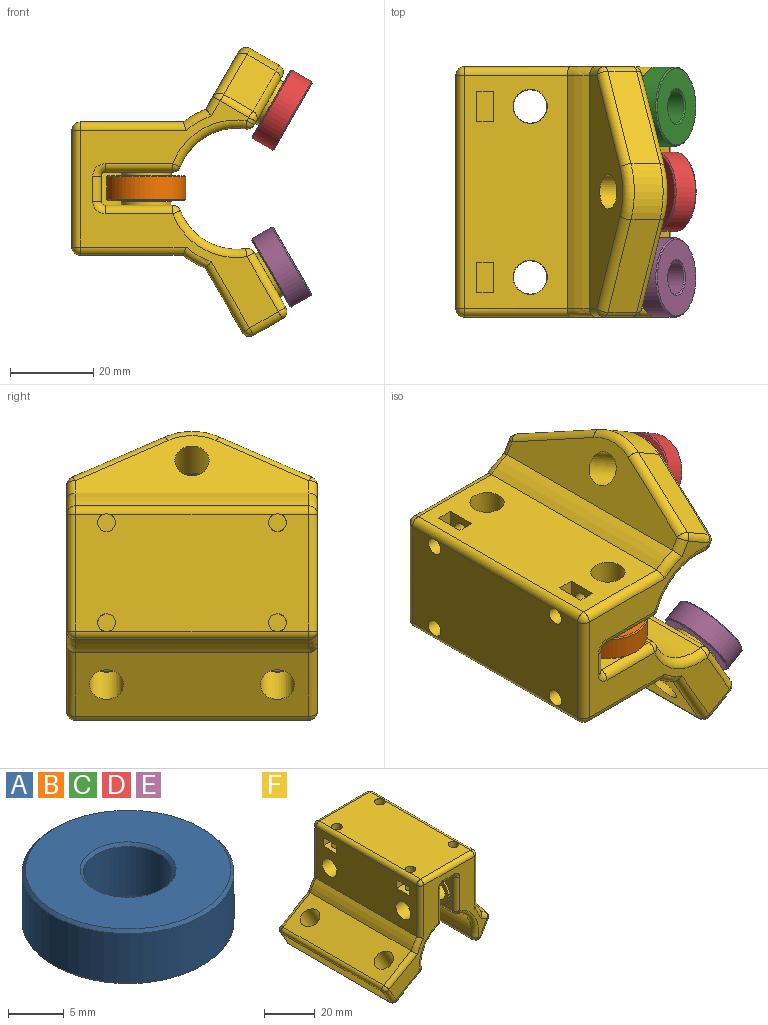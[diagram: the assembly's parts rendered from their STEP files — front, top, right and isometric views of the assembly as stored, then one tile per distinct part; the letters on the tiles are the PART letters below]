
ASSEMBLY  parts=6 mates=5
PART A: 8 faces, bbox 19x19x6 mm
  f0: cylinder r=4mm len=8mm, axis (0,0,-1), area 135.7mm2, adj f4,f6
  f1: cylinder r=9.5mm len=19mm, axis (0,0,-1), area 322.3mm2, adj f5,f7
  f2: plane 18.4x18.4mm, normal (0,0,1), area 207.8mm2, adj f6,f7
  f3: plane 18.4x18.4mm, normal (0,0,-1), area 207.8mm2, adj f4,f5
  f4: cone r=4.3mm half-angle=45deg, axis (0,0,-1), area 11.1mm2, adj f0,f3
  f5: cone r=9.5mm half-angle=45deg, axis (0,0,1), area 24.9mm2, adj f1,f3
  f6: cone r=4mm half-angle=45deg, axis (0,0,1), area 11.1mm2, adj f0,f2
  f7: cone r=9.2mm half-angle=45deg, axis (0,0,-1), area 24.9mm2, adj f1,f2
PART B: same geometry as A
PART C: same geometry as A
PART D: same geometry as A
PART E: same geometry as A
PART F: 155 faces, bbox 70.3x60x51.5 mm
  f0: plane 54.5x47.54mm, normal (0,1,0), area 621.5mm2, adj f104,f108,f112,f114,f115,f117,f118,f119
  f1: plane 54.5x47.54mm, normal (0,-1,0), area 621.5mm2, adj f83,f84,f86,f87,f88,f89,f90,f91
  f2: plane 56x28mm, normal (0,0,1), area 1511.7mm2, adj f67,f68,f73,f74,f97,f124,f144,f147
  f3: plane 56x24.66mm, normal (-1,0,0), area 1217.6mm2, adj f14,f24,f25,f55,f56,f57,f58,f60
  f4: plane 56x24.71mm, normal (1,0,0), area 1220.6mm2, adj f13,f22,f23,f45,f46,f47,f48,f50
  f5: plane 14.58x6mm, normal (0,0,-1), area 87.5mm2, adj f6,f31,f32,f88
  f6: cylinder r=1mm len=15.13mm, axis (0,-1,0), area 23.2mm2, adj f5,f8,f32,f90
  f7: cylinder r=1mm len=15.13mm, axis (0,1,0), area 23.2mm2, adj f9,f17,f32,f119
  f8: plane 56x16.13mm, normal (1,0,0), area 544mm2, adj f6,f27,f30,f32,f41,f43,f92,f112
  f9: plane 56x16.13mm, normal (-1,0,0), area 544mm2, adj f7,f28,f31,f32,f37,f39,f84,f121
  f10: plane 56x15.34mm, normal (-0.5,0,0.87), area 886.2mm2, adj f14,f20,f21,f105,f113,f118
  f11: plane 56x13.11mm, normal (0.5,0,-0.87), area 621.5mm2, adj f26,f33,f35,f100,f107,f108
  f12: plane 56x13.76mm, normal (0.5,0,0.87), area 524.6mm2, adj f13,f77,f91,f130,f134,f135,f136
  f13: cylinder r=20.5mm len=56mm, axis (0,1,0), area 348.4mm2, adj f4,f12,f93,f128
  f14: cylinder r=20.5mm len=56mm, axis (0,1,0), area 348.4mm2, adj f3,f10,f101,f120
  f15: plane 56x6.93mm, normal (-0.87,0,-0.5), area 448mm2, adj f106,f107,f113,f114
  f16: cylinder r=14.5mm len=56mm, axis (0,1,0), area 1095.1mm2, adj f26,f27,f96,f104
  f17: plane 14.58x6mm, normal (0,0,-1), area 87.5mm2, adj f7,f30,f32,f117
  f18: cylinder r=14.5mm len=56mm, axis (0,1,0), area 1097.4mm2, adj f28,f29,f83,f125
  f19: plane 56x11.56mm, normal (-0.5,0,-0.87), area 322.3mm2, adj f29,f78,f87,f129,f139,f140,f141
  f20: cylinder r=4.1mm len=15.36mm, axis (-0.5,0,0.87), area 334.9mm2, adj f10,f36
  f21: cylinder r=4.1mm len=15.36mm, axis (-0.5,0,0.87), area 334.9mm2, adj f10,f34
  f22: cylinder r=4.1mm len=12.85mm, axis (1,0,0), area 331mm2, adj f4,f40
  f23: cylinder r=4.1mm len=12.85mm, axis (1,0,0), area 331mm2, adj f4,f38
  f24: cylinder r=4.1mm len=12.85mm, axis (1,0,0), area 331mm2, adj f3,f44
  f25: cylinder r=4.1mm len=12.85mm, axis (1,0,0), area 331mm2, adj f3,f42
  f26: cylinder r=2mm len=56mm, axis (0,1,0), area 134.1mm2, adj f11,f16,f98,f103
  f27: cylinder r=2mm len=56mm, axis (0,1,0), area 134.2mm2, adj f8,f16,f94,f109
  f28: cylinder r=2mm len=56mm, axis (0,1,0), area 134.2mm2, adj f9,f18,f82,f123
  f29: cylinder r=2mm len=56mm, axis (0,1,0), area 134.4mm2, adj f18,f19,f85,f127
  f30: cylinder r=1mm len=15.13mm, axis (0,-1,0), area 23.2mm2, adj f8,f17,f32,f115
  f31: cylinder r=1mm len=15.13mm, axis (0,1,0), area 23.2mm2, adj f5,f9,f32,f86
  f32: cylinder r=15mm len=26.84mm, axis (1,0,0), area 264.9mm2, adj f5,f6,f7,f8,f9,f17,f30,f31
  f33: cylinder r=6mm len=12mm, axis (-0.5,0,0.87), area 37.7mm2, adj f11,f34
  f34: plane 12x10.39mm, normal (0.5,0,-0.87), area 60.3mm2, adj f21,f33
  f35: cylinder r=6mm len=12mm, axis (-0.5,0,0.87), area 37.7mm2, adj f11,f36
  f36: plane 12x10.39mm, normal (0.5,0,-0.87), area 60.3mm2, adj f20,f35
  f37: cylinder r=6mm len=12mm, axis (1,0,0), area 31.2mm2, adj f9,f38
  f38: plane 12x12mm, normal (-1,0,0), area 60.3mm2, adj f23,f37
  f39: cylinder r=6mm len=12mm, axis (1,0,0), area 31.2mm2, adj f9,f40
  f40: plane 12x12mm, normal (-1,0,0), area 60.3mm2, adj f22,f39
  f41: cylinder r=6mm len=12mm, axis (-1,0,0), area 32.9mm2, adj f8,f42
  f42: plane 12x12mm, normal (1,0,0), area 60.3mm2, adj f25,f41
  f43: cylinder r=6mm len=12mm, axis (-1,0,0), area 32.9mm2, adj f8,f44
  f44: plane 12x12mm, normal (1,0,0), area 60.3mm2, adj f24,f43
  f45: plane 8x4mm, normal (0,1,0), area 32mm2, adj f4,f46,f48,f49
  f46: plane 8x7.2mm, normal (0,0,1), area 43.4mm2, adj f4,f45,f47,f49,f75
  f47: plane 8x4mm, normal (0,-1,0), area 32mm2, adj f4,f46,f48,f49
  f48: plane 8x7.2mm, normal (0,0,-1), area 43.4mm2, adj f4,f45,f47,f49,f74
  f49: plane 7.2x4mm, normal (1,0,0), area 28.8mm2, adj f45,f46,f47,f48
  f50: plane 8x7.2mm, normal (0,0,-1), area 43.4mm2, adj f4,f51,f53,f54,f73
  f51: plane 8x4mm, normal (0,1,0), area 32mm2, adj f4,f50,f52,f54
  f52: plane 8x7.2mm, normal (0,0,1), area 43.4mm2, adj f4,f51,f53,f54,f72
  f53: plane 8x4mm, normal (0,-1,0), area 32mm2, adj f4,f50,f52,f54
  f54: plane 7.2x4mm, normal (1,0,0), area 28.8mm2, adj f50,f51,f52,f53
  f55: plane 8x7.2mm, normal (0,0,1), area 43.4mm2, adj f3,f56,f58,f59,f69
  f56: plane 8x4mm, normal (0,1,0), area 32mm2, adj f3,f55,f57,f59
  f57: plane 8x7.2mm, normal (0,0,-1), area 43.4mm2, adj f3,f56,f58,f59,f68
  f58: plane 8x4mm, normal (0,-1,0), area 32mm2, adj f3,f55,f57,f59
  f59: plane 7.2x4mm, normal (-1,0,0), area 28.8mm2, adj f55,f56,f57,f58
  f60: plane 8x7.2mm, normal (0,0,-1), area 43.4mm2, adj f3,f61,f63,f64,f67
  f61: plane 8x4mm, normal (0,-1,0), area 32mm2, adj f3,f60,f62,f64
  f62: plane 8x7.2mm, normal (0,0,1), area 43.4mm2, adj f3,f61,f63,f64,f66
  f63: plane 8x4mm, normal (0,1,0), area 32mm2, adj f3,f60,f62,f64
  f64: plane 7.2x4mm, normal (-1,0,0), area 28.8mm2, adj f60,f61,f62,f63
  f65: plane 4.25x4.25mm, normal (0,0,1), area 14.2mm2, adj f66
  f66: cylinder r=2.12mm len=4.25mm, axis (0,0,1), area 53.4mm2, adj f62,f65
  f67: cylinder r=2.12mm len=5mm, axis (0,0,1), area 66.8mm2, adj f2,f60,f147
  f68: cylinder r=2.12mm len=5mm, axis (0,0,1), area 66.8mm2, adj f2,f57,f147
  f69: cylinder r=2.12mm len=4.25mm, axis (0,0,1), area 53.4mm2, adj f55,f70
  f70: plane 4.25x4.25mm, normal (0,0,1), area 14.2mm2, adj f69
  f71: plane 4.25x4.25mm, normal (0,0,1), area 14.2mm2, adj f72
  f72: cylinder r=2.12mm len=4.25mm, axis (0,0,1), area 53.4mm2, adj f52,f71
  f73: cylinder r=2.12mm len=5mm, axis (0,0,1), area 66.8mm2, adj f2,f50,f144
  f74: cylinder r=2.12mm len=5mm, axis (0,0,1), area 66.8mm2, adj f2,f48,f144
  f75: cylinder r=2.12mm len=4.25mm, axis (0,0,1), area 53.4mm2, adj f46,f76
  f76: plane 4.25x4.25mm, normal (0,0,1), area 14.2mm2, adj f75
  f77: cylinder r=4.1mm len=15.36mm, axis (0.5,0,0.87), area 334.9mm2, adj f12,f79
  f78: cylinder r=6mm len=12mm, axis (0.5,0,0.87), area 37.7mm2, adj f19,f79
  f79: plane 12x10.39mm, normal (-0.5,0,-0.87), area 60.3mm2, adj f77,f78
  f80: plane 22.19x13.61mm, normal (0.77,-0.45,-0.45), area 198.4mm2, adj f89,f132,f134,f139
  f81: plane 22.19x13.61mm, normal (0.77,0.45,-0.45), area 198.4mm2, adj f131,f132,f136,f141
  f82: sphere r=2mm, area 4.8mm2, adj f28,f83,f84
  f83: torus R=16.5mm, axis (0,-1,0), area 64.6mm2, adj f1,f18,f82,f85
  f84: cylinder r=2mm len=16.13mm, axis (0,0,1), area 50.7mm2, adj f1,f9,f82,f86
  f85: sphere r=2mm, area 4.8mm2, adj f29,f83,f87
  f86: torus R=3mm, axis (0,-1,0), area 8.5mm2, adj f1,f31,f84,f88
  f87: cylinder r=2mm len=2.17mm, axis (-0.87,0,0.5), area 2.8mm2, adj f1,f19,f85,f138
  f88: cylinder r=2mm len=6mm, axis (-1,0,0), area 18.8mm2, adj f1,f5,f86,f90
  f89: cylinder r=2mm len=7.82mm, axis (-0.5,0,-0.87), area 17.7mm2, adj f1,f80,f133,f138
  f90: torus R=3mm, axis (0,-1,0), area 8.5mm2, adj f1,f6,f88,f92
  f91: cylinder r=2mm len=4.59mm, axis (0.87,0,-0.5), area 11.6mm2, adj f1,f12,f93,f133
  f92: cylinder r=2mm len=16.13mm, axis (0,0,-1), area 50.7mm2, adj f1,f8,f90,f94
  f93: torus R=18.5mm, axis (0,-1,0), area 20.4mm2, adj f1,f13,f91,f95
  f94: sphere r=2mm, area 4.8mm2, adj f27,f92,f96
  f95: cylinder r=2mm len=25.43mm, axis (0,0,-1), area 78.4mm2, adj f1,f4,f93,f145
  f96: torus R=16.5mm, axis (0,-1,0), area 64.5mm2, adj f1,f16,f94,f98
  f97: cylinder r=2mm len=28mm, axis (1,0,0), area 88mm2, adj f1,f2,f145,f148
  f98: sphere r=2mm, area 4.8mm2, adj f26,f96,f100
  f99: cylinder r=2mm len=25.38mm, axis (0,0,1), area 78.3mm2, adj f1,f3,f101,f148
  f100: cylinder r=2mm len=14.11mm, axis (-0.87,0,-0.5), area 47.6mm2, adj f1,f11,f98,f102
  f101: torus R=18.5mm, axis (0,-1,0), area 20.4mm2, adj f1,f14,f99,f105
  f102: sphere r=2mm, area 6.3mm2, adj f100,f106,f107
  f103: sphere r=2mm, area 4.8mm2, adj f26,f104,f108
  f104: torus R=16.5mm, axis (0,-1,0), area 64.5mm2, adj f0,f16,f103,f109
  f105: cylinder r=2mm len=16.96mm, axis (0.87,0,0.5), area 56.5mm2, adj f1,f10,f101,f110
  f106: cylinder r=2mm len=7.93mm, axis (-0.5,0,0.87), area 25.1mm2, adj f1,f15,f102,f110
  f107: cylinder r=2mm len=56mm, axis (0,1,0), area 175.9mm2, adj f11,f15,f102,f111
  f108: cylinder r=2mm len=14.11mm, axis (0.87,0,0.5), area 47.6mm2, adj f0,f11,f103,f111
  f109: sphere r=2mm, area 4.8mm2, adj f27,f104,f112
  f110: sphere r=2mm, area 6.3mm2, adj f105,f106,f113
  f111: sphere r=2mm, area 6.3mm2, adj f107,f108,f114
  f112: cylinder r=2mm len=16.13mm, axis (0,0,1), area 50.7mm2, adj f0,f8,f109,f115
  f113: cylinder r=2mm len=56mm, axis (0,1,0), area 175.9mm2, adj f10,f15,f110,f116
  f114: cylinder r=2mm len=7.93mm, axis (0.5,0,-0.87), area 25.1mm2, adj f0,f15,f111,f116
  f115: torus R=3mm, axis (0,-1,0), area 8.5mm2, adj f0,f30,f112,f117
  f116: sphere r=2mm, area 6.3mm2, adj f113,f114,f118
  f117: cylinder r=2mm len=6mm, axis (1,0,0), area 18.8mm2, adj f0,f17,f115,f119
  f118: cylinder r=2mm len=16.96mm, axis (-0.87,0,-0.5), area 56.5mm2, adj f0,f10,f116,f120
  f119: torus R=3mm, axis (0,-1,0), area 8.5mm2, adj f0,f7,f117,f121
  f120: torus R=18.5mm, axis (0,-1,0), area 20.4mm2, adj f0,f14,f118,f122
  f121: cylinder r=2mm len=16.13mm, axis (0,0,-1), area 50.7mm2, adj f0,f9,f119,f123
  f122: cylinder r=2mm len=25.38mm, axis (0,0,-1), area 78.3mm2, adj f0,f3,f120,f146
  f123: sphere r=2mm, area 4.8mm2, adj f28,f121,f125
  f124: cylinder r=2mm len=28mm, axis (-1,0,0), area 88mm2, adj f0,f2,f143,f146
  f125: torus R=16.5mm, axis (0,-1,0), area 64.6mm2, adj f0,f18,f123,f127
  f126: cylinder r=2mm len=25.43mm, axis (0,0,1), area 78.4mm2, adj f0,f4,f128,f143
  f127: sphere r=2mm, area 4.8mm2, adj f29,f125,f129
  f128: torus R=18.5mm, axis (0,-1,0), area 20.4mm2, adj f0,f13,f126,f130
  f129: cylinder r=2mm len=2.17mm, axis (0.87,0,-0.5), area 2.8mm2, adj f0,f19,f127,f142
  f130: cylinder r=2mm len=4.59mm, axis (-0.87,0,0.5), area 11.6mm2, adj f0,f12,f128,f137
  f131: cylinder r=2mm len=7.82mm, axis (0.5,0,0.87), area 17.7mm2, adj f0,f81,f137,f142
  f132: cylinder r=15mm len=13.42mm, axis (0.5,0,0.87), area 111.3mm2, adj f80,f81,f135,f140
  f133: sphere r=2mm, area 4.4mm2, adj f89,f91,f134
  f134: cylinder r=2mm len=23.08mm, axis (0.39,0.89,-0.22), area 77.9mm2, adj f12,f80,f133,f135
  f135: torus R=13mm, axis (0.5,0,0.87), area 41.6mm2, adj f12,f132,f134,f136
  f136: cylinder r=2mm len=23.08mm, axis (-0.39,0.89,0.22), area 77.9mm2, adj f12,f81,f135,f137
  f137: sphere r=2mm, area 4.4mm2, adj f130,f131,f136
  f138: sphere r=2mm, area 4.4mm2, adj f87,f89,f139
  f139: cylinder r=2mm len=23.08mm, axis (-0.39,-0.89,0.22), area 77.9mm2, adj f19,f80,f138,f140
  f140: torus R=13mm, axis (0.5,0,0.87), area 41.6mm2, adj f19,f132,f139,f141
  f141: cylinder r=2mm len=23.08mm, axis (0.39,-0.89,-0.22), area 77.9mm2, adj f19,f81,f140,f142
  f142: sphere r=2mm, area 4.4mm2, adj f129,f131,f141
  f143: sphere r=2mm, area 6.3mm2, adj f124,f126,f144
  f144: cylinder r=2mm len=56mm, axis (0,1,0), area 175.7mm2, adj f2,f4,f73,f74,f143,f145
  f145: sphere r=2mm, area 6.3mm2, adj f95,f97,f144
  f146: sphere r=2mm, area 6.3mm2, adj f122,f124,f147
  f147: cylinder r=2mm len=56mm, axis (0,1,0), area 175.7mm2, adj f2,f3,f67,f68,f146,f148
  f148: sphere r=2mm, area 6.3mm2, adj f97,f99,f147
  f149: cylinder r=12.5mm len=21.11mm, axis (1,0,0), area 200mm2, adj f150,f151,f152,f153,f154
  f150: cylinder r=1mm len=21.11mm, axis (0,1,0), area 32.4mm2, adj f149,f152,f153
  f151: cylinder r=1mm len=21.11mm, axis (0,-1,0), area 32.4mm2, adj f149,f152,f154
  f152: plane 21.11x6mm, normal (0,0,-1), area 126.6mm2, adj f149,f150,f151
  f153: plane 19.7x4.8mm, normal (-1,0,0), area 66mm2, adj f149,f150
  f154: plane 19.7x4.8mm, normal (1,0,0), area 66mm2, adj f149,f151
PLACE A t=(-10.83,59.48,-5.93)mm
PLACE B t=(-10.83,18.48,-5.93)mm
PLACE C rot(axis=(0,-1,0),120deg) t=(24.3,59.48,-20.4)mm
PLACE D rot(axis=(0,-1,0),60deg) t=(24.36,38.98,14.23)mm
PLACE E rot(axis=(0,-1,0),120deg) t=(24.3,18.48,-20.4)mm
PLACE F rot(axis=(0,-1,0),90deg) t=(39.4,38.98,-67.99)mm
MATE fastened F.f22 <-> A.f0  axis (0,0,-1) through (-10.83,59.48,0.07)mm
MATE fastened F.f23 <-> B.f1  axis (0,0,-1) through (-10.83,18.48,0.07)mm
MATE fastened F.f21 <-> C.f1  axis (0.87,0,0.5) through (19.1,59.48,-23.4)mm
MATE fastened F.f77 <-> D.f1  axis (0.87,0,-0.5) through (19.17,38.98,17.23)mm
MATE fastened F.f20 <-> E.f0  axis (0.87,0,0.5) through (19.1,18.48,-23.4)mm
